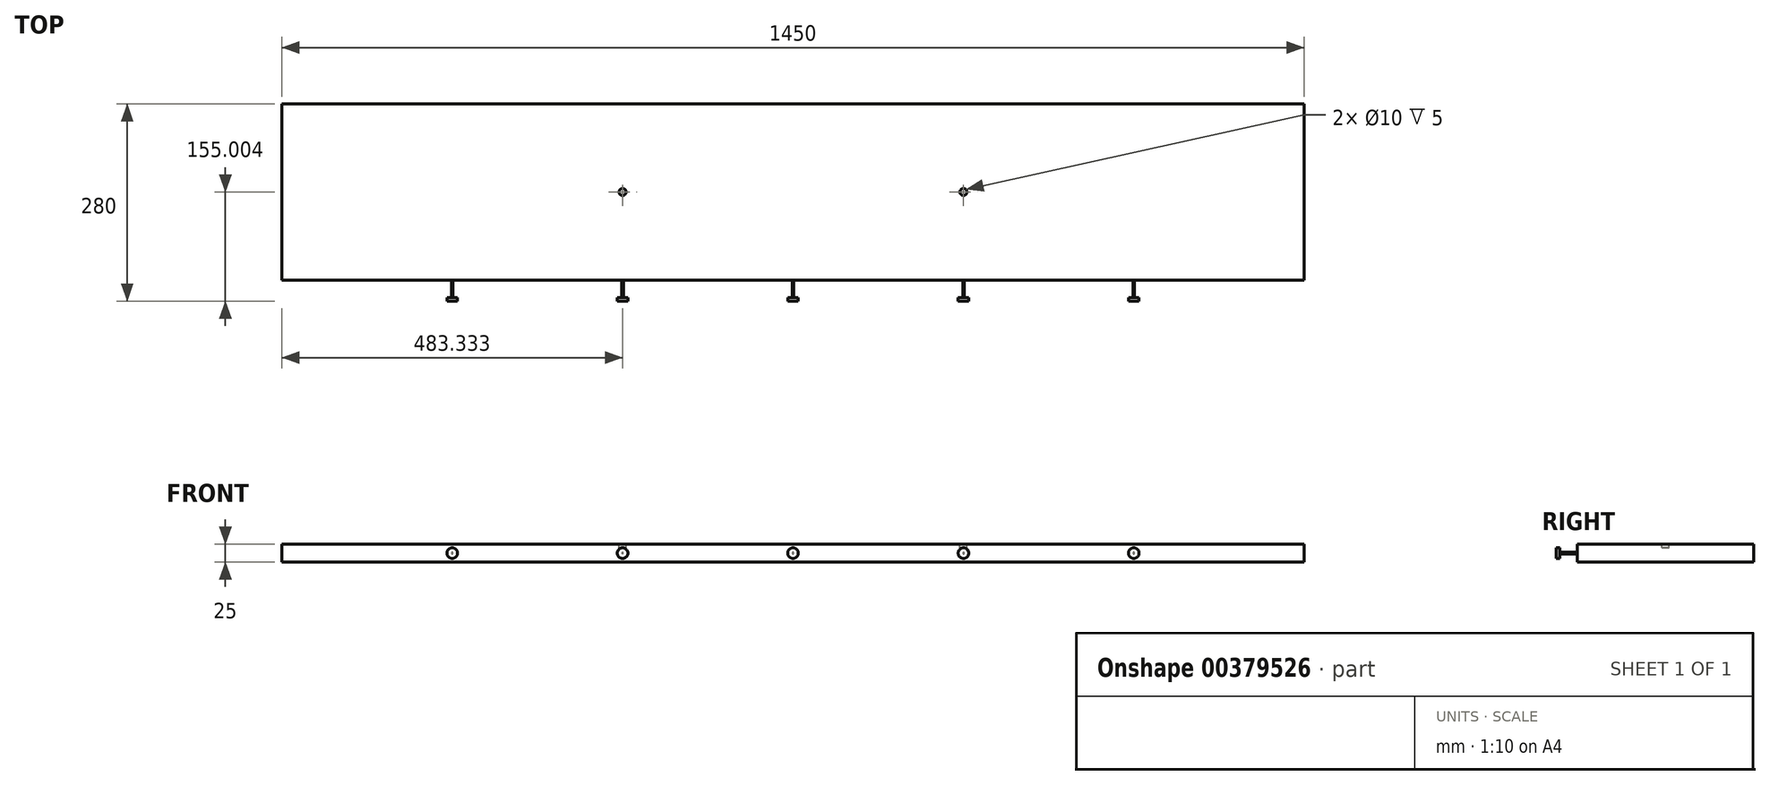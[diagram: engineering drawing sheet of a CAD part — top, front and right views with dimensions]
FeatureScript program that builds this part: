
annotation { "Feature Type Name" : "Feature", "Feature Type Description" : "" }
export const myFeature = defineFeature(function(context is Context, id is Id, definition is map)
    precondition{}
    {
        {
            var Q0;
            Q0=qCreatedBy(makeId("Top.planeOp"),FACE);
            var sketch = newSketch(context, id + "F0", { "sketchPlane" : qUnion([Q0])});
            skLineSegment(sketch, "E0.bottom", {"start": v(-725, -111.9) * mm, "end": v(725, -111.9) * mm});
            skLineSegment(sketch, "E0.top", {"start": v(-725, -361.9) * mm, "end": v(725, -361.9) * mm});
            skLineSegment(sketch, "E0.left", {"start": v(-725, -111.9) * mm, "end": v(-725, -361.9) * mm});
            skLineSegment(sketch, "E0.right", {"start": v(725, -111.9) * mm, "end": v(725, -361.9) * mm});
            skLineSegment(sketch, "E1", {"start": v(0, -111.9) * mm, "end": v(0, -361.9) * mm, "construction": true});
            skSolve(sketch);
        }
        {
            var Q0;
            Q0=makeQuery(id+"F0.imprint","IMPRINT",FACE,{"disambiguationData":[TD([[makeQuery(id+"F0.imprint","IMPRINT",EDGE,{"derivedFrom":sQuery(id+"F0.wireOp",EDGE,"E0.bottom")}),-1.0]])]});
            extrude(context, id + "F1", {"entities" : qUnion([Q0]), "depth" : 25 * mm});
        }
        {
            var Q0;
            Q0=makeQuery(id+"F1.opExtrude","SWEPT_FACE",FACE,{"disambiguationData":[OSD([sQuery(id+"F0.wireOp",EDGE,"E0.top")])]});
            var sketch = newSketch(context, id + "F2", { "sketchPlane" : qUnion([Q0])});
            skLineSegment(sketch, "E2", {"start": v(-725, 25) * mm, "end": v(-483.33, 25) * mm, "construction": true});
            skLineSegment(sketch, "E3", {"start": v(-483.33, 25) * mm, "end": v(-241.67, 25) * mm, "construction": true});
            skLineSegment(sketch, "E4", {"start": v(-241.67, 25) * mm, "end": v(0, 25) * mm, "construction": true});
            skLineSegment(sketch, "E5", {"start": v(-483.33, 25) * mm, "end": v(-483.33, 0) * mm, "construction": true});
            skLineSegment(sketch, "E6", {"start": v(-241.67, 25) * mm, "end": v(-241.67, 0) * mm, "construction": true});
            skLineSegment(sketch, "E7", {"start": v(0, 25) * mm, "end": v(0, 0) * mm, "construction": true});
            skLineSegment(sketch, "E8.MirrorCS", {"start": v(241.67, 25) * mm, "end": v(241.67, 0) * mm, "construction": true});
            skLineSegment(sketch, "E9.MirrorCS", {"start": v(483.33, 25) * mm, "end": v(483.33, 0) * mm, "construction": true});
            skLineSegment(sketch, "E10.MirrorCS", {"start": v(241.67, 25) * mm, "end": v(0, 25) * mm, "construction": true});
            skLineSegment(sketch, "E11.MirrorCS", {"start": v(483.33, 25) * mm, "end": v(241.67, 25) * mm, "construction": true});
            skLineSegment(sketch, "E12.MirrorCS", {"start": v(725, 25) * mm, "end": v(483.33, 25) * mm, "construction": true});
            skCircle(sketch, "E13", {"center": v(-483.33, 12.5) * mm, "radius": 1 * mm});
            skCircle(sketch, "E14", {"center": v(-241.67, 12.5) * mm, "radius": 1 * mm});
            skCircle(sketch, "E15", {"center": v(0, 12.5) * mm, "radius": 1 * mm});
            skCircle(sketch, "E16", {"center": v(241.67, 12.5) * mm, "radius": 1 * mm});
            skCircle(sketch, "E17", {"center": v(483.33, 12.5) * mm, "radius": 1 * mm});
            skSolve(sketch);
        }
        {
            var Q0;
            Q0=makeQuery(id+"F2.imprint","IMPRINT",FACE,{"disambiguationData":[TD([[makeQuery(id+"F2.imprint","IMPRINT",EDGE,{"derivedFrom":sQuery(id+"F2.wireOp",EDGE,"E13")}),1.0]])]});
            var Q1;
            Q1=makeQuery(id+"F2.imprint","IMPRINT",FACE,{"disambiguationData":[TD([[makeQuery(id+"F2.imprint","IMPRINT",EDGE,{"derivedFrom":sQuery(id+"F2.wireOp",EDGE,"E14")}),1.0]])]});
            var Q2;
            Q2=makeQuery(id+"F2.imprint","IMPRINT",FACE,{"disambiguationData":[TD([[makeQuery(id+"F2.imprint","IMPRINT",EDGE,{"derivedFrom":sQuery(id+"F2.wireOp",EDGE,"E15")}),1.0]])]});
            var Q3;
            Q3=makeQuery(id+"F2.imprint","IMPRINT",FACE,{"disambiguationData":[TD([[makeQuery(id+"F2.imprint","IMPRINT",EDGE,{"derivedFrom":sQuery(id+"F2.wireOp",EDGE,"E16")}),1.0]])]});
            var Q4;
            Q4=makeQuery(id+"F2.imprint","IMPRINT",FACE,{"disambiguationData":[TD([[makeQuery(id+"F2.imprint","IMPRINT",EDGE,{"derivedFrom":sQuery(id+"F2.wireOp",EDGE,"E17")}),1.0]])]});
            extrude(context, id + "F3", {"entities" : qUnion([Q0, Q1, Q2, Q3, Q4]), "operationType" : NewBodyOperationType.ADD, "depth" : 25 * mm});
        }
        {
            var Q0;
            Q0=makeQuery(id+"F1.opExtrude","SWEPT_FACE",FACE,{"disambiguationData":[OSD([sQuery(id+"F0.wireOp",EDGE,"E0.top")])]});
            cPlane(context, id + "F4", {"entities" : qUnion([Q0]), "cplaneType" : CPlaneType.OFFSET, "offset" : 25 * mm, "width" : 150 * mm, "height" : 150 * mm});
        }
        {
            var Q0;
            Q0=qCreatedBy(id+"F4.planeOp",FACE);
            var sketch = newSketch(context, id + "F5", { "sketchPlane" : qUnion([Q0])});
            skLineSegment(sketch, "E18", {"start": v(0, 0) * mm, "end": v(-241.67, 0) * mm, "construction": true});
            skLineSegment(sketch, "E19", {"start": v(-241.67, 0) * mm, "end": v(-483.33, 0) * mm, "construction": true});
            skLineSegment(sketch, "E20", {"start": v(-483.33, 0) * mm, "end": v(-725, 0) * mm, "construction": true});
            skLineSegment(sketch, "E21", {"start": v(0, 0) * mm, "end": v(0, 25) * mm, "construction": true});
            skLineSegment(sketch, "E22", {"start": v(-241.67, 0) * mm, "end": v(-241.67, 25) * mm, "construction": true});
            skLineSegment(sketch, "E23", {"start": v(-483.33, 0) * mm, "end": v(-483.33, 25) * mm, "construction": true});
            skCircle(sketch, "E24", {"center": v(-483.33, 12.5) * mm, "radius": 7.5 * mm});
            skCircle(sketch, "E25", {"center": v(-241.67, 12.5) * mm, "radius": 7.5 * mm});
            skCircle(sketch, "E26", {"center": v(0, 12.5) * mm, "radius": 7.5 * mm});
            skCircle(sketch, "E27.MirrorC", {"center": v(241.67, 12.5) * mm, "radius": 7.5 * mm});
            skCircle(sketch, "E28.MirrorC", {"center": v(483.33, 12.5) * mm, "radius": 7.5 * mm});
            skSolve(sketch);
        }
        {
            var Q0;
            Q0 = qSketchRegion(id + "F5", true);
            extrude(context, id + "F6", {"entities" : qUnion([Q0]), "operationType" : NewBodyOperationType.ADD, "depth" : 5 * mm});
        }
        {
            var Q0;
            Q0=makeQuery(id+"F1.opExtrude","CAP_FACE",FACE,{"disambiguationData":[OSD([sQuery(id+"F0.wireOp",EDGE,"E0.bottom"),sQuery(id+"F0.wireOp",EDGE,"E0.top"),sQuery(id+"F0.wireOp",EDGE,"E0.left"),sQuery(id+"F0.wireOp",EDGE,"E0.right")])],"isStart":false});
            var sketch = newSketch(context, id + "F7", { "sketchPlane" : qUnion([Q0])});
            skLineSegment(sketch, "E29", {"start": v(-725, -111.9) * mm, "end": v(-241.67, -111.9) * mm, "construction": true});
            skLineSegment(sketch, "E30", {"start": v(-241.67, -111.9) * mm, "end": v(241.67, -111.9) * mm, "construction": true});
            skLineSegment(sketch, "E31", {"start": v(241.67, -111.9) * mm, "end": v(725, -111.9) * mm, "construction": true});
            skLineSegment(sketch, "E32", {"start": v(-241.67, -111.9) * mm, "end": v(-241.67, -361.9) * mm, "construction": true});
            skLineSegment(sketch, "E33", {"start": v(241.67, -111.9) * mm, "end": v(241.67, -361.9) * mm, "construction": true});
            skCircle(sketch, "E34", {"center": v(-241.67, -236.9) * mm, "radius": 5 * mm});
            skCircle(sketch, "E35", {"center": v(241.67, -236.9) * mm, "radius": 5 * mm});
            skSolve(sketch);
        }
        {
            var Q0;
            Q0=makeQuery(id+"F7.imprint","IMPRINT",FACE,{"disambiguationData":[TD([[makeQuery(id+"F7.imprint","IMPRINT",EDGE,{"derivedFrom":sQuery(id+"F7.wireOp",EDGE,"E34")}),1.0]])]});
            var Q1;
            Q1=makeQuery(id+"F7.imprint","IMPRINT",FACE,{"disambiguationData":[TD([[makeQuery(id+"F7.imprint","IMPRINT",EDGE,{"derivedFrom":sQuery(id+"F7.wireOp",EDGE,"E35")}),1.0]])]});
            extrude(context, id + "F8", {"entities" : qUnion([Q0, Q1]), "operationType" : NewBodyOperationType.REMOVE, "oppositeDirection" : true, "depth" : 5 * mm});
        }
    });
